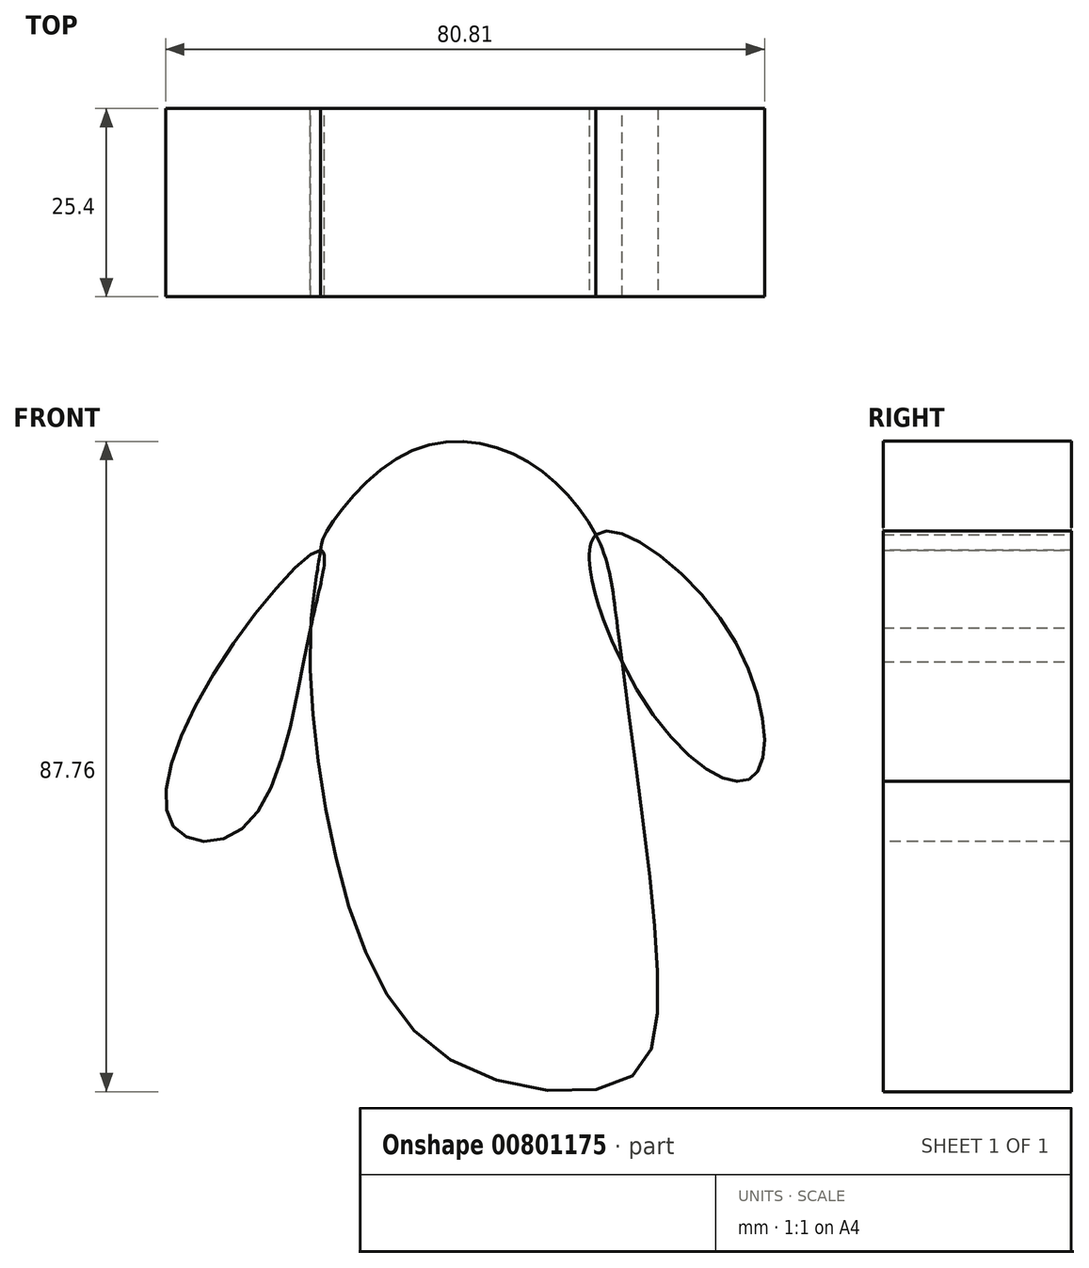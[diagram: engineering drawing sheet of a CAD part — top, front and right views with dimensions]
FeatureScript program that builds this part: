
annotation { "Feature Type Name" : "Feature", "Feature Type Description" : "" }
export const myFeature = defineFeature(function(context is Context, id is Id, definition is map)
    precondition{}
    {
        {
            var Q0;
            Q0=qCreatedBy(makeId("Front.planeOp"),FACE);
            var sketch = newSketch(context, id + "F0", { "sketchPlane" : qUnion([Q0])});
            skFitSpline(sketch, "E0", {"points": [v(-25.7, 39.53) * mm, v(-15.45, 50.15) * mm, v(0, 50.34) * mm, v(10.9, 39.53) * mm, v(13.75, 27.59) * mm, v(17.35, 0) * mm, v(19.24, -23.04) * mm, v(15.26, -33.84) * mm, v(-6.54, -32.52) * mm, v(-20.2, -16.78) * mm, v(-26.26, 6.92) * mm, v(-27.59, 27.02) * mm, v(-26.26, 37.45) * mm, v(-25.7, 39.53) * mm]});
            skFitSpline(sketch, "E1", {"points": [v(-27.59, 27.02) * mm, v(-36.69, 0) * mm, v(-45.98, 0) * mm, v(-41.62, 19.24) * mm, v(-26.26, 37.45) * mm, v(-27.59, 27.02) * mm]});
            skFitSpline(sketch, "E2", {"points": [v(10.9, 39.53) * mm, v(19.62, 13.94) * mm, v(32.14, 6.92) * mm, v(28.53, 27.02) * mm, v(10.9, 39.53) * mm]});
            skSolve(sketch);
        }
        {
            var Q0;
            {var subQ0=sQuery(id+"F0.wireOp",EDGE,"E2");var subQ1=sQuery(id+"F0.wireOp",EDGE,"E0");var subQ2=makeQuery(id+"F0.imprint","INTERSECT",VERTEX,{"disambiguationData":[OD(0.0)],"derivedFrom":[subQ1,subQ0]});Q0=makeQuery(id+"F0.imprint","IMPRINT",FACE,{"disambiguationData":[TD([[makeQuery(id+"F0.imprint","IMPRINT",EDGE,{"disambiguationData":[TD([[subQ2,-1.0]])],"derivedFrom":subQ1}),-1.0]])]});}
            extrude(context, id + "F1", {"entities" : qUnion([Q0]), "depth" : 25.4 * mm, "offsetDistance" : 25.4 * mm});
        }
        {
            var Q0;
            {var subQ0=sQuery(id+"F0.wireOp",EDGE,"E2");var subQ1=sQuery(id+"F0.wireOp",EDGE,"E0");var subQ2=makeQuery(id+"F0.imprint","INTERSECT",VERTEX,{"disambiguationData":[OD(0.0)],"derivedFrom":[subQ1,subQ0]});Q0=makeQuery(id+"F0.imprint","IMPRINT",FACE,{"disambiguationData":[TD([[makeQuery(id+"F0.imprint","IMPRINT",EDGE,{"disambiguationData":[TD([[subQ2,1.0]])],"derivedFrom":subQ1}),1.0]])]});}
            var Q1;
            {var subQ0=sQuery(id+"F0.wireOp",EDGE,"E1");var subQ1=sQuery(id+"F0.wireOp",EDGE,"E0");var subQ2=makeQuery(id+"F0.imprint","INTERSECT",VERTEX,{"disambiguationData":[OD(0.0)],"derivedFrom":[subQ1,subQ0]});Q1=makeQuery(id+"F0.imprint","IMPRINT",FACE,{"disambiguationData":[TD([[makeQuery(id+"F0.imprint","IMPRINT",EDGE,{"disambiguationData":[TD([[subQ2,-1.0]])],"derivedFrom":subQ1}),1.0]])]});}
            extrude(context, id + "F2", {"entities" : qUnion([Q0, Q1]), "depth" : 25.4 * mm, "offsetDistance" : 25.4 * mm});
        }
    });
